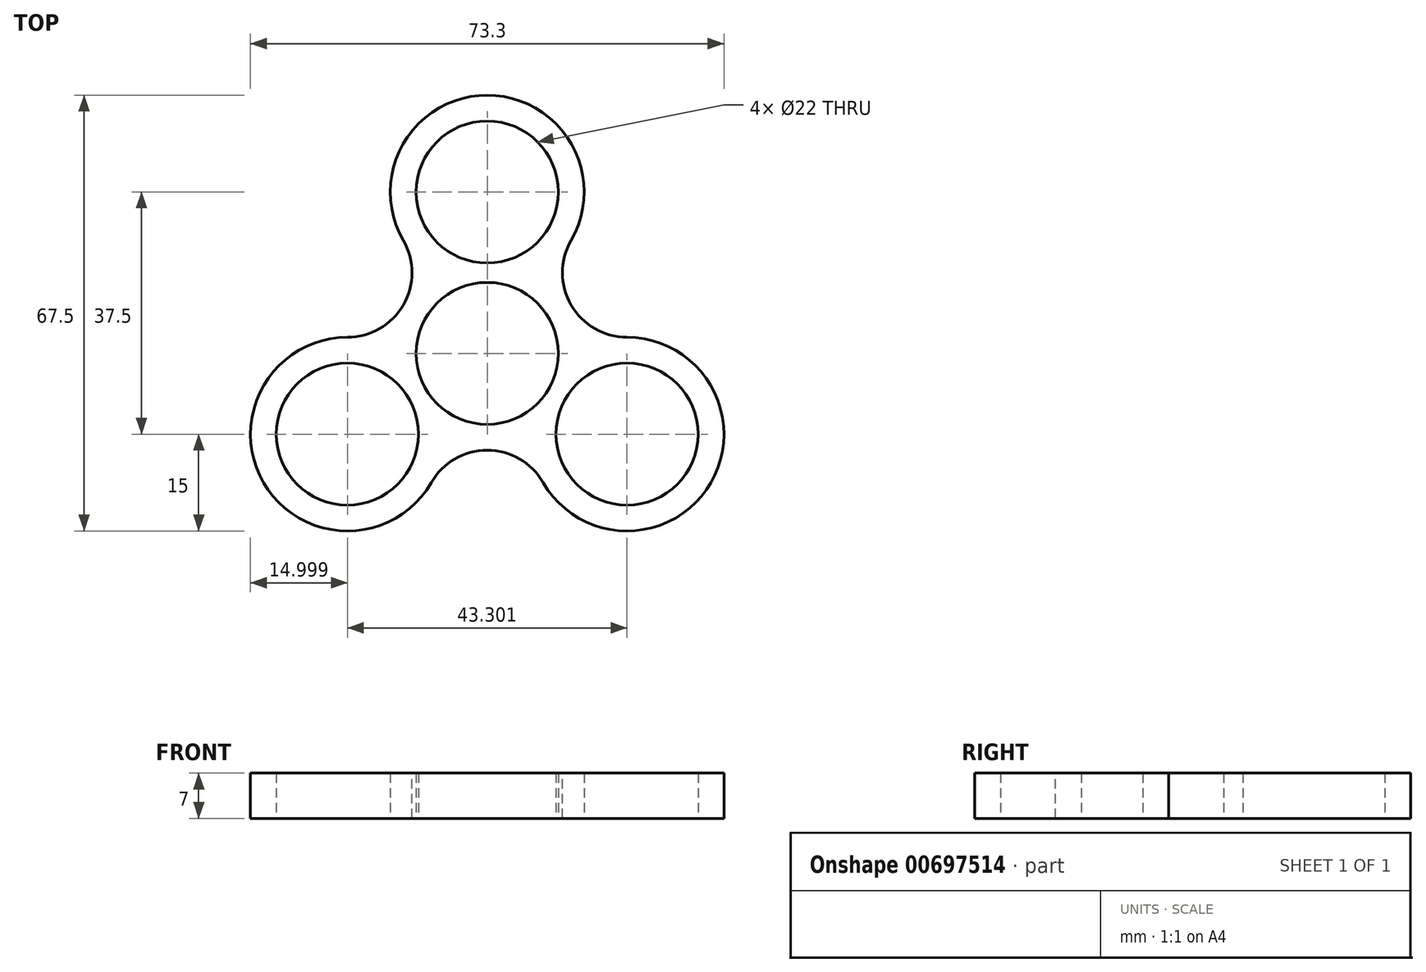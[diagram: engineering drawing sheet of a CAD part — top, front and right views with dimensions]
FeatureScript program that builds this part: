
annotation { "Feature Type Name" : "Feature", "Feature Type Description" : "" }
export const myFeature = defineFeature(function(context is Context, id is Id, definition is map)
    precondition{}
    {
        {
            var Q0;
            Q0=qCreatedBy(makeId("Top.planeOp"),FACE);
            var sketch = newSketch(context, id + "F0", { "sketchPlane" : qUnion([Q0])});
            skCircle(sketch, "E0", {"center": v(0, 0) * mm, "radius": 11 * mm});
            skArc(sketch, "E1", {"start": v(-8.3, 12.5) * mm, "mid": v(-13, 7.5) * mm, "end": v(-14.97, 0.93) * mm});
            skCircle(sketch, "E2", {"center": v(0, 0) * mm, "radius": 25 * mm, "construction": true});
            skLineSegment(sketch, "E3", {"start": v(0, 0) * mm, "end": v(0, 25) * mm, "construction": true});
            skLineSegment(sketch, "E4", {"start": v(0, 0) * mm, "end": v(21.65, -12.5) * mm, "construction": true});
            skLineSegment(sketch, "E5", {"start": v(0, 0) * mm, "end": v(-21.65, -12.5) * mm, "construction": true});
            skCircle(sketch, "E6", {"center": v(0, 25) * mm, "radius": 11 * mm});
            skArc(sketch, "E7", {"start": v(8.3, 12.5) * mm, "mid": v(0, 40) * mm, "end": v(-8.3, 12.5) * mm});
            skCircle(sketch, "E8", {"center": v(21.65, -12.5) * mm, "radius": 11 * mm});
            skCircle(sketch, "E9", {"center": v(-21.65, -12.5) * mm, "radius": 11 * mm});
            skArc(sketch, "E10.trimOffspring", {"start": v(14.97, 0.93) * mm, "mid": v(13, 7.5) * mm, "end": v(8.3, 12.5) * mm});
            skArc(sketch, "E11.trimOffspring", {"start": v(6.68, -13.43) * mm, "mid": v(34.64, -20) * mm, "end": v(14.97, 0.93) * mm});
            skArc(sketch, "E12.trimOffspring", {"start": v(-6.68, -13.43) * mm, "mid": v(0, -15) * mm, "end": v(6.68, -13.43) * mm});
            skArc(sketch, "E13.trimOffspring", {"start": v(-14.97, 0.93) * mm, "mid": v(-34.64, -20) * mm, "end": v(-6.68, -13.43) * mm});
            skSolve(sketch);
        }
        {
            var Q0;
            Q0=makeQuery(id+"F0.imprint","IMPRINT",FACE,{"disambiguationData":[TD([[makeQuery(id+"F0.imprint","IMPRINT",EDGE,{"derivedFrom":sQuery(id+"F0.wireOp",EDGE,"E0")}),-1.0]])]});
            extrude(context, id + "F1", {"entities" : qUnion([Q0]), "depth" : 7 * mm, "offsetDistance" : 25 * mm});
        }
        {
            var Q0;
            Q0=makeQuery(id+"F1.opExtrude","SWEPT_EDGE",EDGE,{"disambiguationData":[OSD([sQuery(id+"F0.wireOp",EDGE,"E1"),sQuery(id+"F0.wireOp",EDGE,"E7")])]});
            var Q1;
            Q1=makeQuery(id+"F1.opExtrude","SWEPT_EDGE",EDGE,{"disambiguationData":[OSD([sQuery(id+"F0.wireOp",EDGE,"E1"),sQuery(id+"F0.wireOp",EDGE,"E13.trimOffspring")])]});
            var Q2;
            Q2=makeQuery(id+"F1.opExtrude","SWEPT_EDGE",EDGE,{"disambiguationData":[OSD([sQuery(id+"F0.wireOp",EDGE,"E12.trimOffspring"),sQuery(id+"F0.wireOp",EDGE,"E13.trimOffspring")])]});
            var Q3;
            Q3=makeQuery(id+"F1.opExtrude","SWEPT_EDGE",EDGE,{"disambiguationData":[OSD([sQuery(id+"F0.wireOp",EDGE,"E11.trimOffspring"),sQuery(id+"F0.wireOp",EDGE,"E12.trimOffspring")])]});
            var Q4;
            Q4=makeQuery(id+"F1.opExtrude","SWEPT_EDGE",EDGE,{"disambiguationData":[OSD([sQuery(id+"F0.wireOp",EDGE,"E10.trimOffspring"),sQuery(id+"F0.wireOp",EDGE,"E11.trimOffspring")])]});
            var Q5;
            Q5=makeQuery(id+"F1.opExtrude","SWEPT_EDGE",EDGE,{"disambiguationData":[OSD([sQuery(id+"F0.wireOp",EDGE,"E7"),sQuery(id+"F0.wireOp",EDGE,"E10.trimOffspring")])]});
            fillet(context, id + "F2", {"entities" : qUnion([Q0, Q1, Q2, Q3, Q4, Q5]), "radius" : 10 * mm, "tangentPropagation" : true, "allowEdgeOverflow" : false});
        }
    });
